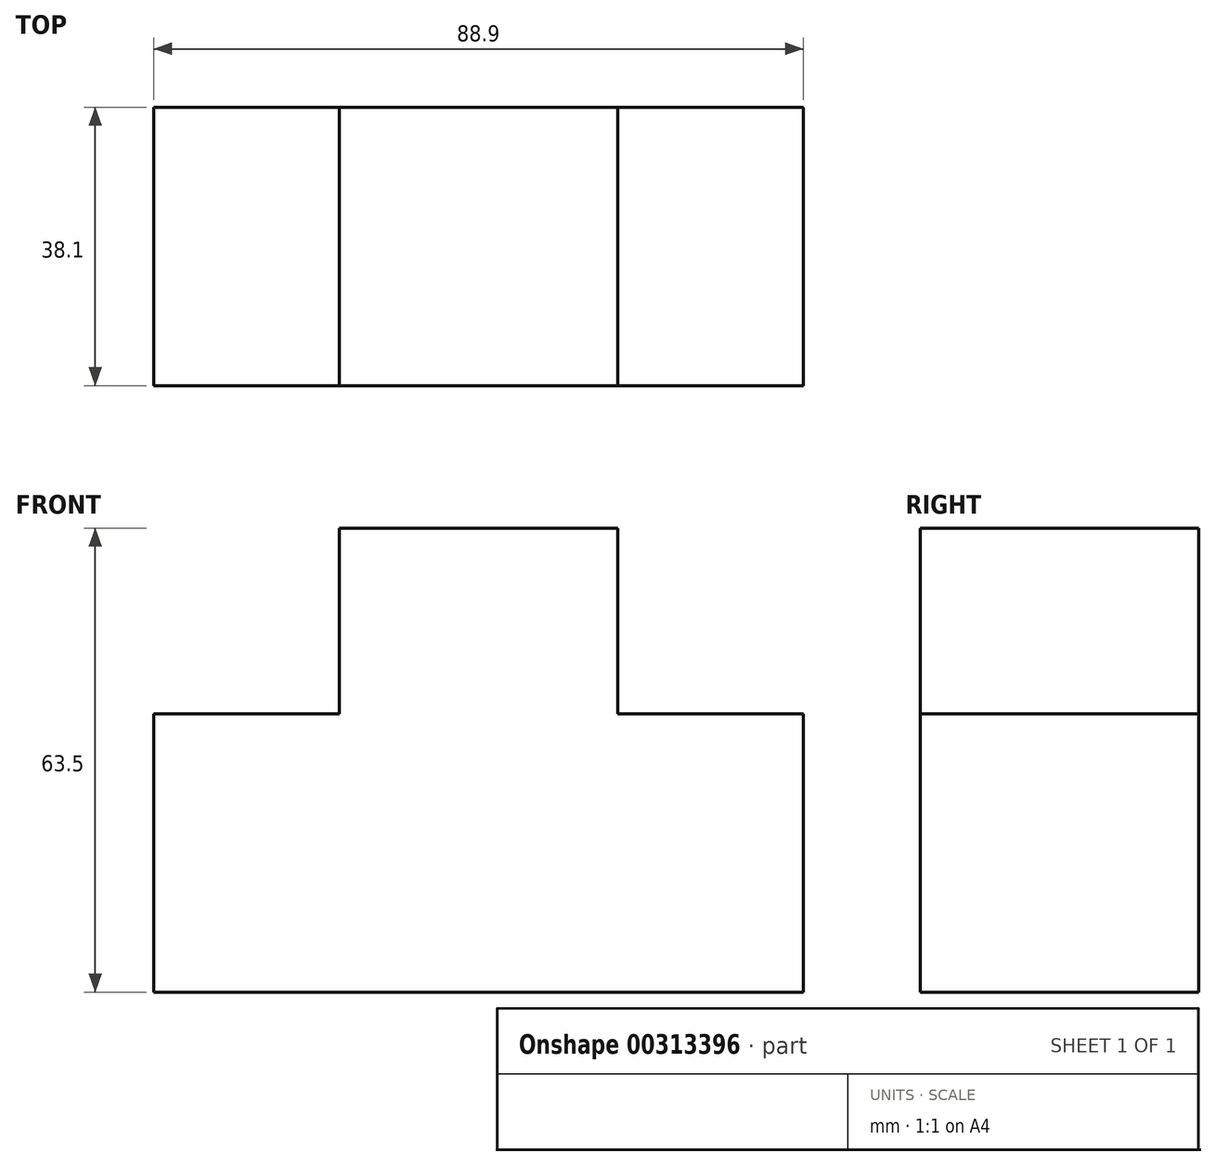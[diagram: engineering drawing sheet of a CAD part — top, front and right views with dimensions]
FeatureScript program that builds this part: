
annotation { "Feature Type Name" : "Feature", "Feature Type Description" : "" }
export const myFeature = defineFeature(function(context is Context, id is Id, definition is map)
    precondition{}
    {
        {
            var Q0;
            Q0=qCreatedBy(makeId("Front.planeOp"),FACE);
            var sketch = newSketch(context, id + "F0", { "sketchPlane" : qUnion([Q0])});
            skLineSegment(sketch, "E0", {"start": v(-43.79, -50.7) * mm, "end": v(45.11, -50.7) * mm});
            skLineSegment(sketch, "E1", {"start": v(45.11, -50.7) * mm, "end": v(45.11, -12.6) * mm});
            skLineSegment(sketch, "E2", {"start": v(45.11, -12.6) * mm, "end": v(19.71, -12.6) * mm});
            skLineSegment(sketch, "E3", {"start": v(19.71, -12.6) * mm, "end": v(19.71, 12.8) * mm});
            skLineSegment(sketch, "E4", {"start": v(19.71, 12.8) * mm, "end": v(-18.39, 12.8) * mm});
            skLineSegment(sketch, "E5", {"start": v(-18.39, 12.8) * mm, "end": v(-18.39, -12.6) * mm});
            skLineSegment(sketch, "E6", {"start": v(-18.39, -12.6) * mm, "end": v(-43.79, -12.6) * mm});
            skLineSegment(sketch, "E7", {"start": v(-43.79, -12.6) * mm, "end": v(-43.79, -50.7) * mm});
            skSolve(sketch);
        }
        {
            var Q0;
            Q0=makeQuery(id+"F0.imprint","IMPRINT",FACE,{"disambiguationData":[TD([[makeQuery(id+"F0.imprint","IMPRINT",EDGE,{"derivedFrom":sQuery(id+"F0.wireOp",EDGE,"E0")}),1.0]])]});
            extrude(context, id + "F1", {"entities" : qUnion([Q0]), "depth" : 38.1 * mm});
        }
    });
